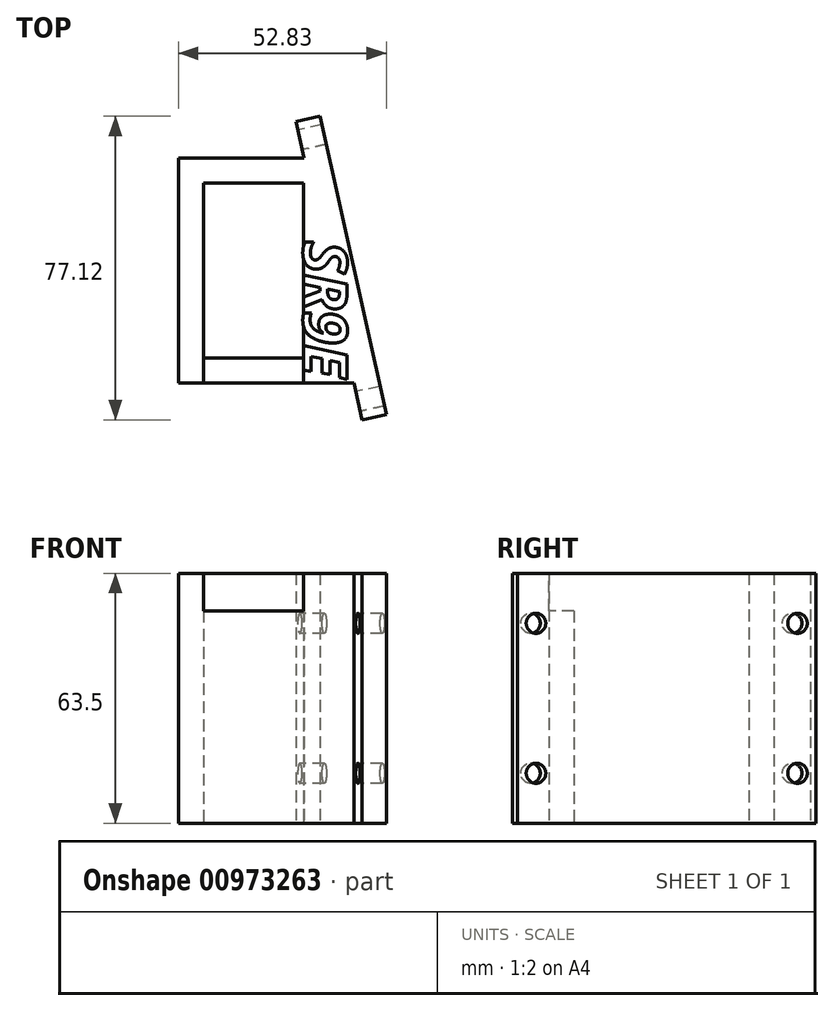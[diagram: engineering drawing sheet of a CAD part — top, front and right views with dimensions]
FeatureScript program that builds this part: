
annotation { "Feature Type Name" : "Feature", "Feature Type Description" : "" }
export const myFeature = defineFeature(function(context is Context, id is Id, definition is map)
    precondition{}
    {
        {
            var Q0;
            Q0=qCreatedBy(makeId("Top.planeOp"),FACE);
            var sketch = newSketch(context, id + "F0", { "sketchPlane" : qUnion([Q0])});
            skLineSegment(sketch, "E0.bottom", {"start": v(0, 0) * mm, "end": v(25.4, 0) * mm});
            skLineSegment(sketch, "E0.top", {"start": v(0, 44.45) * mm, "end": v(25.4, 44.45) * mm});
            skLineSegment(sketch, "E0.left", {"start": v(0, 0) * mm, "end": v(0, 44.45) * mm});
            skLineSegment(sketch, "E0.right", {"start": v(25.4, 0) * mm, "end": v(25.4, 44.45) * mm});
            skLineSegment(sketch, "E1.bottom", {"start": v(-6.35, -6.35) * mm, "end": v(31.75, -6.35) * mm});
            skLineSegment(sketch, "E1.top", {"start": v(-6.35, 50.8) * mm, "end": v(25.55, 50.8) * mm});
            skLineSegment(sketch, "E1.left", {"start": v(-6.35, -6.35) * mm, "end": v(-6.35, 50.8) * mm});
            skLineSegment(sketch, "E2", {"start": v(31.75, -6.35) * mm, "end": v(38.22, -6.35) * mm});
            skLineSegment(sketch, "E3", {"start": v(32.05, 50.8) * mm, "end": v(44.72, -6.35) * mm});
            skLineSegment(sketch, "E4", {"start": v(32.05, 50.8) * mm, "end": v(29.6, 61.86) * mm});
            skLineSegment(sketch, "E5", {"start": v(44.72, -6.35) * mm, "end": v(46.48, -14.27) * mm});
            skLineSegment(sketch, "E6", {"start": v(46.48, -14.27) * mm, "end": v(40.28, -15.65) * mm});
            skLineSegment(sketch, "E7", {"start": v(40.28, -15.65) * mm, "end": v(38.22, -6.35) * mm});
            skLineSegment(sketch, "E8", {"start": v(29.69, 61.47) * mm, "end": v(23.49, 60.1) * mm});
            skLineSegment(sketch, "E9", {"start": v(23.49, 60.1) * mm, "end": v(25.55, 50.8) * mm});
            skSolve(sketch);
        }
        {
            var Q0;
            Q0=makeQuery(id+"F0.imprint","IMPRINT",FACE,{"disambiguationData":[TD([[makeQuery(id+"F0.imprint","IMPRINT",EDGE,{"derivedFrom":sQuery(id+"F0.wireOp",EDGE,"E0.bottom")}),-1.0]])]});
            extrude(context, id + "F1", {"entities" : qUnion([Q0]), "depth" : 63.5 * mm, "offsetDistance" : 25.4 * mm});
        }
        {
            var Q0;
            Q0=makeQuery(id+"F1.opExtrude","CAP_FACE",FACE,{"disambiguationData":[OSD([sQuery(id+"F0.wireOp",EDGE,"E0.bottom"),sQuery(id+"F0.wireOp",EDGE,"E0.top"),sQuery(id+"F0.wireOp",EDGE,"E0.left"),sQuery(id+"F0.wireOp",EDGE,"E0.right"),sQuery(id+"F0.wireOp",EDGE,"E1.bottom"),sQuery(id+"F0.wireOp",EDGE,"E1.top"),sQuery(id+"F0.wireOp",EDGE,"E1.left"),sQuery(id+"F0.wireOp",EDGE,"E1.right")])],"isStart":false});
            var sketch = newSketch(context, id + "F2", { "sketchPlane" : qUnion([Q0])});
            skLineSegment(sketch, "E10", {"start": v(0, 0) * mm, "end": v(0, -6.35) * mm});
            skLineSegment(sketch, "E11", {"start": v(25.4, 0) * mm, "end": v(25.4, -6.35) * mm});
            skSolve(sketch);
        }
        {
            var Q0;
            Q0 = qSketchRegion(id + "F2", true);
            var Q1;
            {var subQ0=sQuery(id+"F2.wireOp",EDGE,"E10");Q1=makeQuery(id+"F2.imprint","IMPRINT",FACE,{"disambiguationData":[TD([[makeQuery(id+"F2.imprint","IMPRINT",EDGE,{"derivedFrom":subQ0}),1.0]])]});}
            extrude(context, id + "F3", {"entities" : qUnion([Q0, Q1]), "operationType" : NewBodyOperationType.REMOVE, "oppositeDirection" : true, "depth" : 9.52 * mm, "offsetDistance" : 25.4 * mm});
        }
        {
            var Q0;
            Q0=makeQuery(id+"F1.opExtrude","CAP_FACE",FACE,{"disambiguationData":[OSD([sQuery(id+"F0.wireOp",EDGE,"E0.bottom"),sQuery(id+"F0.wireOp",EDGE,"E0.top"),sQuery(id+"F0.wireOp",EDGE,"E0.left"),sQuery(id+"F0.wireOp",EDGE,"E0.right"),sQuery(id+"F0.wireOp",EDGE,"E1.bottom"),sQuery(id+"F0.wireOp",EDGE,"E1.top"),sQuery(id+"F0.wireOp",EDGE,"E1.left"),sQuery(id+"F0.wireOp",EDGE,"E2"),sQuery(id+"F0.wireOp",EDGE,"E3"),sQuery(id+"F0.wireOp",EDGE,"E4"),sQuery(id+"F0.wireOp",EDGE,"E5"),sQuery(id+"F0.wireOp",EDGE,"E6"),sQuery(id+"F0.wireOp",EDGE,"E7"),sQuery(id+"F0.wireOp",EDGE,"E8"),sQuery(id+"F0.wireOp",EDGE,"E9")])],"isStart":false});
            var sketch = newSketch(context, id + "F4", { "sketchPlane" : qUnion([Q0])});
            skText(sketch, "E12", { "text": "SR9E", "fontName": "OpenSans-BoldItalic.ttf"});
            const initialGuessF4  = {"E12": [0.0254, 0.0298, 0, -1, 0.01117]};
            skSetInitialGuess(sketch, initialGuessF4);
            skSolve(sketch);
        }
        {
            var Q0;
            Q0=makeQuery(id+"F4.imprint","IMPRINT",FACE,{"disambiguationData":[TD([[makeQuery(id+"F4.imprint","IMPRINT",EDGE,{"derivedFrom":sQuery(id+"F4.wireOp",EDGE,"E12.sketch_text.stroke-24")}),-1.0]])]});
            var Q1;
            Q1 = qSketchRegion(id + "F4", true);
            extrude(context, id + "F5", {"entities" : qUnion([Q0, Q1]), "operationType" : NewBodyOperationType.ADD, "depth" : .125 / 50.8 * mm, "offsetDistance" : 25.4 * mm});
        }
        {
            var Q0;
            Q0=makeQuery(id+"F1.opExtrude","SWEPT_FACE",FACE,{"disambiguationData":[OSD([sQuery(id+"F0.wireOp",EDGE,"E7")])]});
            var sketch = newSketch(context, id + "F6", { "sketchPlane" : qUnion([Q0])});
            skCircle(sketch, "E13", {"center": v(19.23, 50.8) * mm, "radius": 2.55 * mm});
            skCircle(sketch, "E14", {"center": v(19.23, 12.7) * mm, "radius": 2.55 * mm});
            skSolve(sketch);
        }
        {
            var Q0;
            Q0 = qSketchRegion(id + "F6", true);
            extrude(context, id + "F7", {"entities" : qUnion([Q0]), "operationType" : NewBodyOperationType.REMOVE, "oppositeDirection" : true, "depth" : 25.4 * mm, "offsetDistance" : 25.4 * mm});
        }
        {
            var Q0;
            Q0=makeQuery(id+"F1.opExtrude","SWEPT_FACE",FACE,{"disambiguationData":[OSD([sQuery(id+"F0.wireOp",EDGE,"E9")])]});
            var sketch = newSketch(context, id + "F8", { "sketchPlane" : qUnion([Q0])});
            skCircle(sketch, "E15", {"center": v(-48.83, 50.8) * mm, "radius": 2.55 * mm});
            skCircle(sketch, "E16", {"center": v(-48.83, 12.7) * mm, "radius": 2.55 * mm});
            skSolve(sketch);
        }
        {
            var Q0;
            Q0 = qSketchRegion(id + "F8", true);
            extrude(context, id + "F9", {"entities" : qUnion([Q0]), "operationType" : NewBodyOperationType.REMOVE, "oppositeDirection" : true, "depth" : 25.4 * mm, "offsetDistance" : 25.4 * mm});
        }
    });
